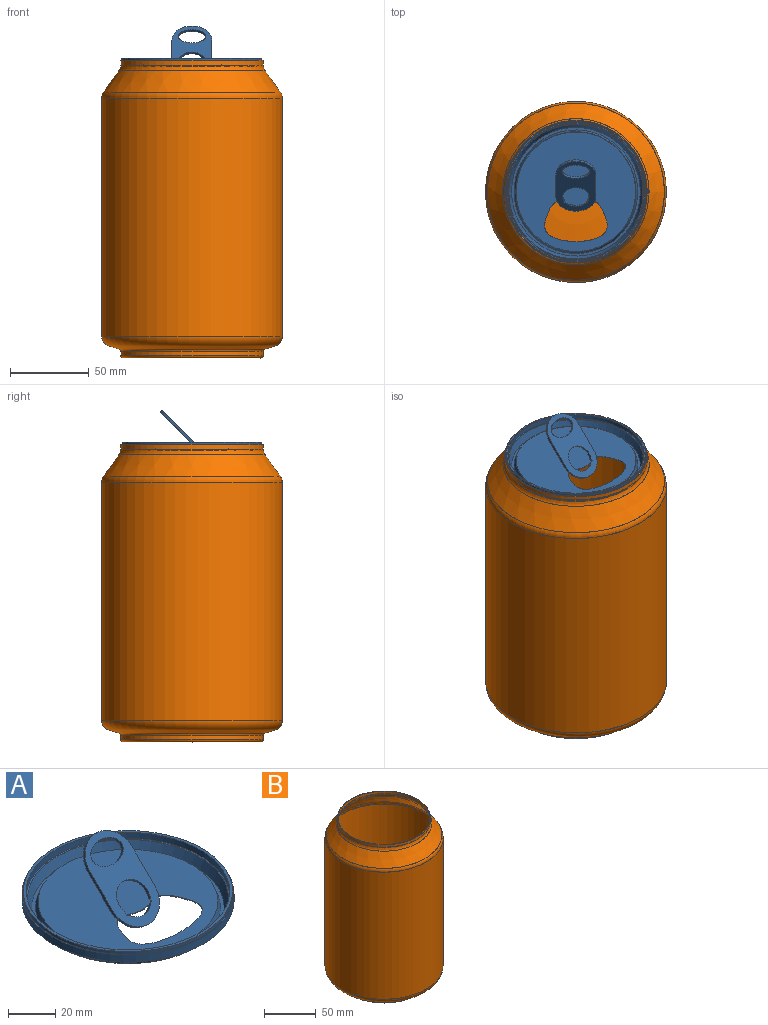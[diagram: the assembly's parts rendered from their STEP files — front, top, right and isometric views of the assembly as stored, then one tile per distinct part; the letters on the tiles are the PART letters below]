
ASSEMBLY  parts=2 mates=1
PART A: 35 faces, bbox 89.9x89.9x32.6 mm
  f0: plane 75.71x75.71mm, normal (0,0,-1), area 3655mm2, adj f2,f3,f4,f5,f6,f25,f27,f29
  f1: plane 76.21x76.21mm, normal (0,0,1), area 3711.8mm2, adj f2,f3,f4,f5,f7,f26,f28,f29
  f2: extruded ~25.4x19.84mm, area 15.1mm2, adj f0,f1,f4,f29
  f3: extruded ~7.65x1.85mm, area 2.6mm2, adj f0,f1,f5,f30
  f4: extruded ~25.4x19.84mm, area 15.1mm2, adj f0,f1,f2,f29
  f5: extruded ~7.65x1.85mm, area 2.6mm2, adj f0,f1,f3,f30
  f6: cone r=38.94mm half-angle=20deg, axis (0,0,-1), area 765.9mm2, adj f0,f24
  f7: cone r=38.1mm half-angle=20deg, axis (0,0,-1), area 770.9mm2, adj f1,f8
  f8: plane 81.55x81.55mm, normal (0,0,1), area 398.8mm2, adj f7,f9
  f9: cone r=40.77mm half-angle=20deg, axis (0,0,1), area 1373.7mm2, adj f8,f10
  f10: cone r=42.57mm half-angle=73.6deg, axis (0,0,1), area 150.4mm2, adj f9,f11
  f11: cylinder r=43.1mm len=86.21mm, axis (0,0,-1), area 859.9mm2, adj f10,f12
  f12: plane 88.75x88.75mm, normal (0,0,1), area 349mm2, adj f11,f13
  f13: cylinder r=44.37mm len=88.75mm, axis (0,0,-1), area 1327.8mm2, adj f12,f14
  f14: plane 89.15x89.15mm, normal (0,0,1), area 56.8mm2, adj f13,f15
  f15: cylinder r=44.58mm len=89.15mm, axis (0,0,-1), area 947.6mm2, adj f14,f16
  f16: plane 89.87x89.87mm, normal (0,0,1), area 100mm2, adj f15,f17
  f17: cylinder r=44.93mm len=89.87mm, axis (0,0,-1), area 1055.6mm2, adj f16,f18
  f18: plane 89.87x89.87mm, normal (0,0,-1), area 255.5mm2, adj f17,f19
  f19: cylinder r=44.02mm len=88.04mm, axis (0,0,-1), area 1317.2mm2, adj f18,f20
  f20: plane 88.04x88.04mm, normal (0,0,-1), area 153.6mm2, adj f19,f21
  f21: cylinder r=43.46mm len=86.92mm, axis (0,0,-1), area 842.5mm2, adj f20,f22
  f22: cone r=43.46mm half-angle=73.6deg, axis (0,0,1), area 174.9mm2, adj f21,f23
  f23: cone r=42.84mm half-angle=20deg, axis (0,0,1), area 1400.5mm2, adj f22,f24
  f24: plane 82.05x82.05mm, normal (0,0,-1), area 523.9mm2, adj f6,f23
  f25: cylinder r=8.33mm len=14.95mm, axis (0,-0.71,0.71), area 26.5mm2, adj f0,f27,f30
  f26: cylinder r=8.33mm len=16.66mm, axis (0,-0.71,0.71), area 54.7mm2, adj f1,f28,f30
  f27: plane 24.31x6.38mm, normal (0,0.71,-0.71), area 111.5mm2, adj f0,f25,f29
  f28: plane 25.4x24.7mm, normal (0,0.71,-0.71), area 495.3mm2, adj f1,f26,f29,f31,f32,f33,f34
  f29: cylinder r=12.7mm len=25.4mm, axis (0,-0.71,0.71), area 62.2mm2, adj f0,f1,f2,f4,f27,f28,f30,f32
  f30: plane 31.44x31.44mm, normal (0,-0.71,0.71), area 610.9mm2, adj f0,f1,f3,f5,f25,f26,f29,f31
  f31: cylinder r=12.7mm len=25.4mm, axis (0,-0.71,0.71), area 63.3mm2, adj f28,f30,f32,f34
  f32: plane 14.59x14.59mm, normal (1,0,0), area 30.2mm2, adj f28,f29,f30,f31
  f33: extruded ~17.57x9.38mm, area 73.7mm2, adj f28,f30
  f34: plane 14.59x14.59mm, normal (-1,0,0), area 30.2mm2, adj f28,f29,f30,f31
PART B: 37 faces, bbox 124.1x124.1x188.9 mm
  f0: cylinder r=44.58mm len=89.15mm, axis (0,0,1), area 747mm2, adj f1,f17
  f1: torus R=44.83mm, axis (0,0,1), area 112mm2, adj f0,f2
  f2: plane 89.92x89.92mm, normal (0,0,1), area 35.8mm2, adj f1,f3
  f3: torus R=44.96mm, axis (0,0,1), area 113.1mm2, adj f2,f4
  f4: cylinder r=45.21mm len=90.42mm, axis (0,0,1), area 829.8mm2, adj f3,f5
  f5: torus R=51.56mm, axis (0,0,1), area 1135.5mm2, adj f4,f6
  f6: cone r=56.15mm half-angle=35.7deg, axis (0,0,-1), area 5370.1mm2, adj f5,f7
  f7: torus R=50.99mm, axis (0,0,1), area 1417.3mm2, adj f6,f8
  f8: cylinder r=57.34mm len=151.01mm, axis (0,0,1), area 54408.7mm2, adj f7,f9
  f9: torus R=50.99mm, axis (0,0,1), area 2844mm2, adj f8,f10
  f10: cone r=46.34mm half-angle=73.3deg, axis (0,0,1), area 2107.5mm2, adj f9,f11
  f11: torus R=46.8mm, axis (0,0,1), area 581.7mm2, adj f10,f12
  f12: cylinder r=45.21mm len=90.42mm, axis (0,0,1), area 743.1mm2, adj f11,f13
  f13: torus R=43.62mm, axis (0,0,1), area 1367mm2, adj f12,f14
  f14: cylinder r=42.04mm len=84.07mm, axis (0,0,1), area 586.6mm2, adj f13,f15
  f15: torus R=40.45mm, axis (0,0,1), area 599.3mm2, adj f14,f16
  f16: sphere r=327.74mm, area 5210.4mm2, adj f15
  f17: torus R=44.32mm, axis (0,0,1), area 111.5mm2, adj f0,f18
  f18: cylinder r=44.32mm len=88.65mm, axis (0,0,-1), area 28.3mm2, adj f17,f36
  f19: cylinder r=44.68mm len=89.36mm, axis (0,0,1), area 748.7mm2, adj f20,f36
  f20: torus R=44.83mm, axis (0,0,1), area 67.3mm2, adj f19,f21
  f21: plane 89.92x89.92mm, normal (0,0,-1), area 35.8mm2, adj f20,f22
  f22: torus R=44.96mm, axis (0,0,1), area 67.8mm2, adj f21,f23
  f23: cylinder r=45.11mm len=90.22mm, axis (0,0,1), area 827.9mm2, adj f22,f24
  f24: torus R=51.56mm, axis (0,0,1), area 1151.2mm2, adj f23,f25
  f25: cone r=56.06mm half-angle=35.7deg, axis (0,0,-1), area 5361.5mm2, adj f24,f26
  f26: torus R=50.99mm, axis (0,0,1), area 1392.3mm2, adj f25,f27
  f27: cylinder r=57.24mm len=151.01mm, axis (0,0,1), area 54312.3mm2, adj f26,f28
  f28: torus R=50.99mm, axis (0,0,1), area 2794.7mm2, adj f27,f29
  f29: cone r=46.31mm half-angle=73.3deg, axis (0,0,1), area 2106.3mm2, adj f28,f30
  f30: torus R=46.8mm, axis (0,0,1), area 617.9mm2, adj f29,f31
  f31: cylinder r=45.11mm len=90.22mm, axis (0,0,1), area 741.5mm2, adj f30,f32
  f32: torus R=43.62mm, axis (0,0,1), area 1279.5mm2, adj f31,f33
  f33: cylinder r=42.14mm len=84.28mm, axis (0,0,1), area 588mm2, adj f32,f34
  f34: torus R=40.45mm, axis (0,0,1), area 638.7mm2, adj f33,f35
  f35: sphere r=327.84mm, area 5213.7mm2, adj f34
  f36: torus R=44.32mm, axis (0,0,1), area 156.4mm2, adj f18,f19
PLACE A t=(-14.75,66.35,201.97)mm
PLACE B t=(-14.75,66.35,22.71)mm
MATE cylindrical A.f6 <-> B.f0  axis (0,0,-1) through (-14.75,66.35,204)mm
